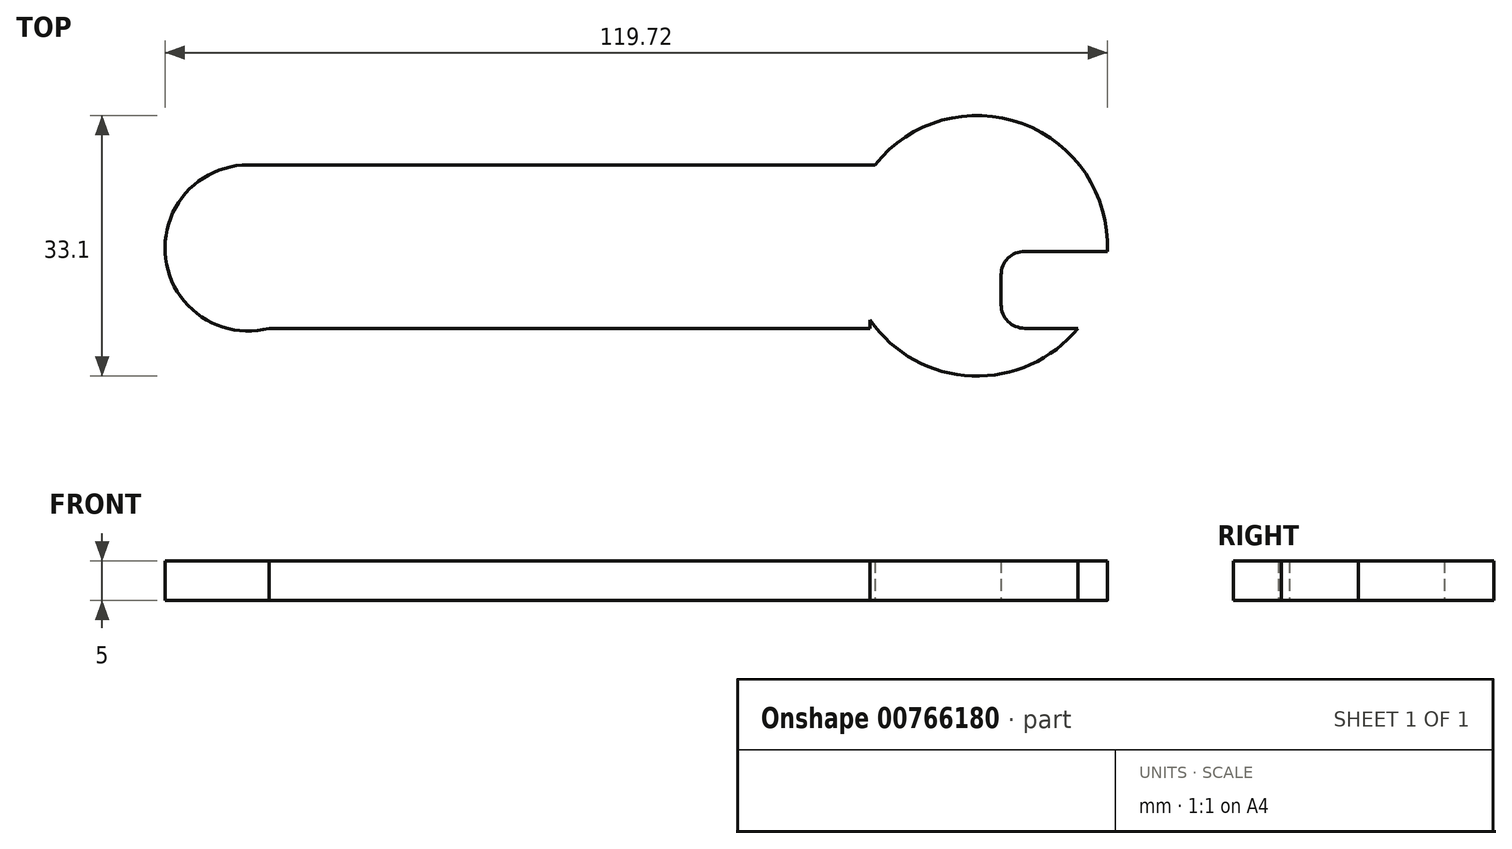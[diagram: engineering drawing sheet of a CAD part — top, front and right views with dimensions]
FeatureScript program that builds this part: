
annotation { "Feature Type Name" : "Feature", "Feature Type Description" : "" }
export const myFeature = defineFeature(function(context is Context, id is Id, definition is map)
    precondition{}
    {
        {
            var Q0;
            Q0=qCreatedBy(makeId("Top.planeOp"),FACE);
            var sketch = newSketch(context, id + "F0", { "sketchPlane" : qUnion([Q0])});
            skLineSegment(sketch, "E0.bottom", {"start": v(-52.97, 11.43) * mm, "end": v(26.67, 11.43) * mm});
            skLineSegment(sketch, "E0.top", {"start": v(-50.29, -9.32) * mm, "end": v(26.03, -9.32) * mm});
            skLineSegment(sketch, "E0.right", {"start": v(26.06, -8.3) * mm, "end": v(26.03, -9.32) * mm});
            skArc(sketch, "E1", {"start": v(56.18, 0.45) * mm, "mid": v(24.19, 7.06) * mm, "end": v(52.45, -9.32) * mm});
            skLineSegment(sketch, "E2.bottom", {"start": v(56.18, 0.45) * mm, "end": v(45.7, 0.45) * mm});
            skLineSegment(sketch, "E2.top", {"start": v(52.45, -9.32) * mm, "end": v(45.7, -9.32) * mm});
            skLineSegment(sketch, "E2.right", {"start": v(42.7, -2.55) * mm, "end": v(42.7, -6.32) * mm});
            skArc(sketch, "E3", {"start": v(-52.97, 11.43) * mm, "mid": v(-63.43, -0.47) * mm, "end": v(-50.29, -9.32) * mm});
            skPoint(sketch, "E4.visualSharp", {"position": v(42.7, 0.45) * mm});
            skArc(sketch, "E4.filletArc", {"start": v(45.7, 0.45) * mm, "mid": v(43.57, -0.43) * mm, "end": v(42.7, -2.55) * mm});
            skPoint(sketch, "E5.visualSharp", {"position": v(42.7, -9.32) * mm});
            skArc(sketch, "E5.filletArc", {"start": v(42.7, -6.32) * mm, "mid": v(43.57, -8.45) * mm, "end": v(45.7, -9.32) * mm});
            skSolve(sketch);
        }
        {
            var Q0;
            Q0 = qSketchRegion(id + "F0", true);
            extrude(context, id + "F1", {"entities" : qUnion([Q0]), "depth" : 5 * mm, "offsetDistance" : 25 * mm});
        }
    });
